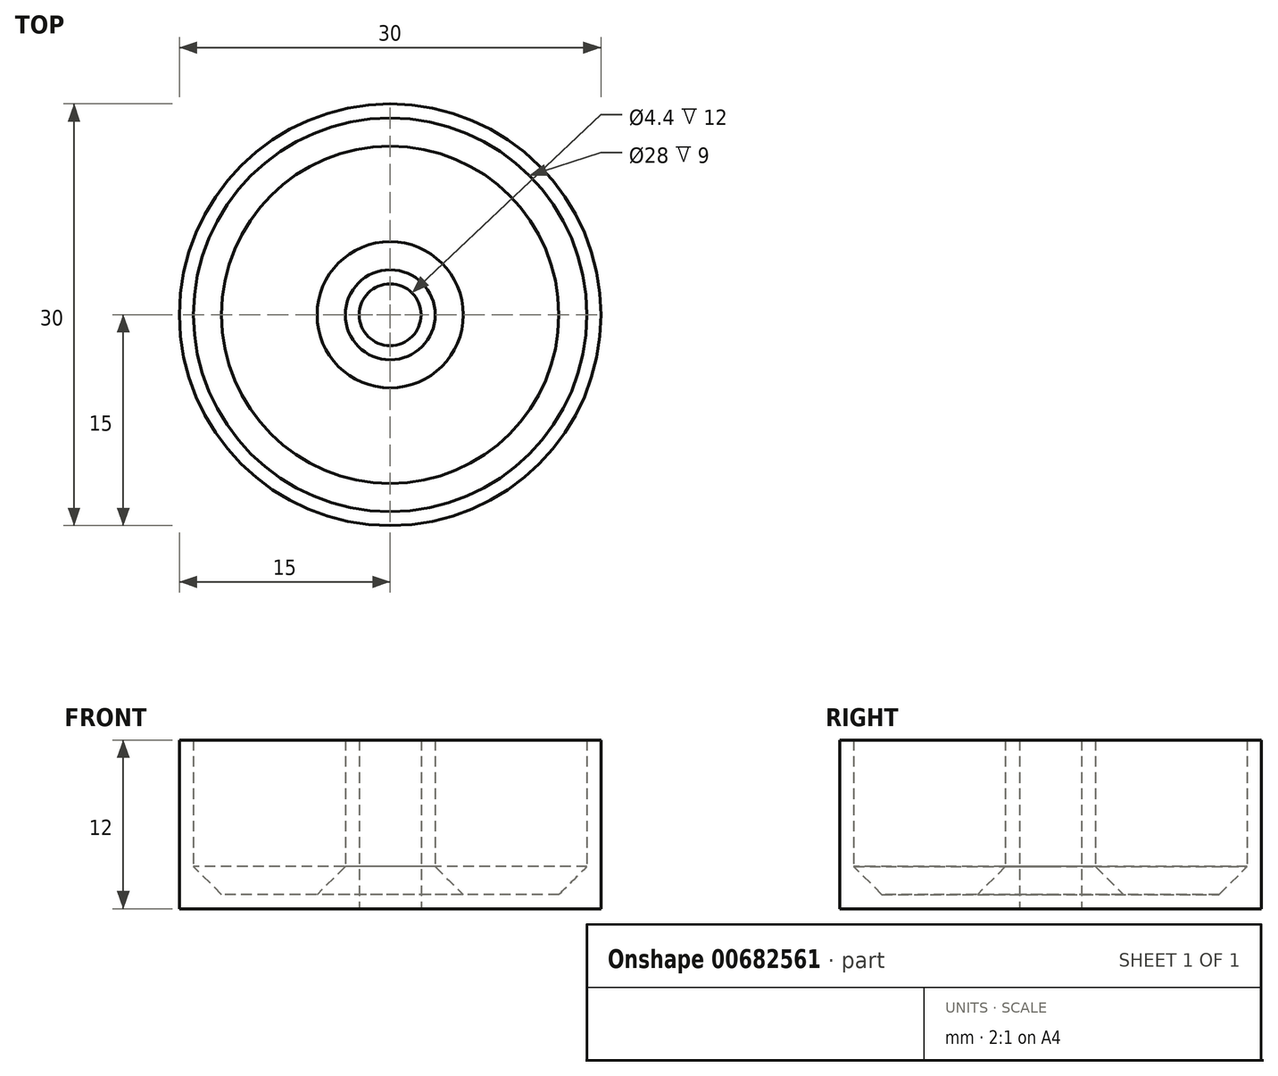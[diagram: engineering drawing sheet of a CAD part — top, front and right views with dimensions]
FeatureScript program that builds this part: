
annotation { "Feature Type Name" : "Feature", "Feature Type Description" : "" }
export const myFeature = defineFeature(function(context is Context, id is Id, definition is map)
    precondition{}
    {
        {
            var Q0;
            Q0=qCreatedBy(makeId("Top.planeOp"),FACE);
            var sketch = newSketch(context, id + "F0", { "sketchPlane" : qUnion([Q0])});
            skCircle(sketch, "E0", {"center": v(0, 0) * mm, "radius": 15 * mm});
            skCircle(sketch, "E1", {"center": v(0, 0) * mm, "radius": 2.2 * mm});
            skSolve(sketch);
        }
        {
            var Q0;
            Q0=makeQuery(id+"F0.imprint","IMPRINT",FACE,{"disambiguationData":[TD([[makeQuery(id+"F0.imprint","IMPRINT",EDGE,{"derivedFrom":sQuery(id+"F0.wireOp",EDGE,"E0")}),1.0]])]});
            extrude(context, id + "F1", {"entities" : qUnion([Q0]), "depth" : 12 * mm, "offsetDistance" : 25 * mm});
        }
        {
            var Q0;
            Q0=makeQuery(id+"F1.opExtrude","CAP_FACE",FACE,{"disambiguationData":[OSD([sQuery(id+"F0.wireOp",EDGE,"E0"),sQuery(id+"F0.wireOp",EDGE,"E1")])],"isStart":false});
            shell(context, id + "F2", {"entities" : qUnion([Q0]), "thickness" : 1 * mm});
        }
        {
            var Q0;
            {var subQ0=sQuery(id+"F0.wireOp",EDGE,"E0");Q0=makeQuery(id+"F2.opShell","OFFSET_EDGE",EDGE,{"disambiguationData":[OSD([subQ0]),TDD([makeQuery(id+"F1.opExtrude","CAP_EDGE",EDGE,{"disambiguationData":[OSD([subQ0])],"isStart":true})])]});}
            var Q1;
            {var subQ0=sQuery(id+"F0.wireOp",EDGE,"E1");Q1=makeQuery(id+"F2.opShell","OFFSET_EDGE",EDGE,{"disambiguationData":[OSD([subQ0]),TDD([makeQuery(id+"F1.opExtrude","CAP_EDGE",EDGE,{"disambiguationData":[OSD([subQ0])],"isStart":true})])]});}
            chamfer(context, id + "F3", {"entities" : qUnion([Q0, Q1]), "width" : 2 * mm, "tangentPropagation" : true});
        }
    });
